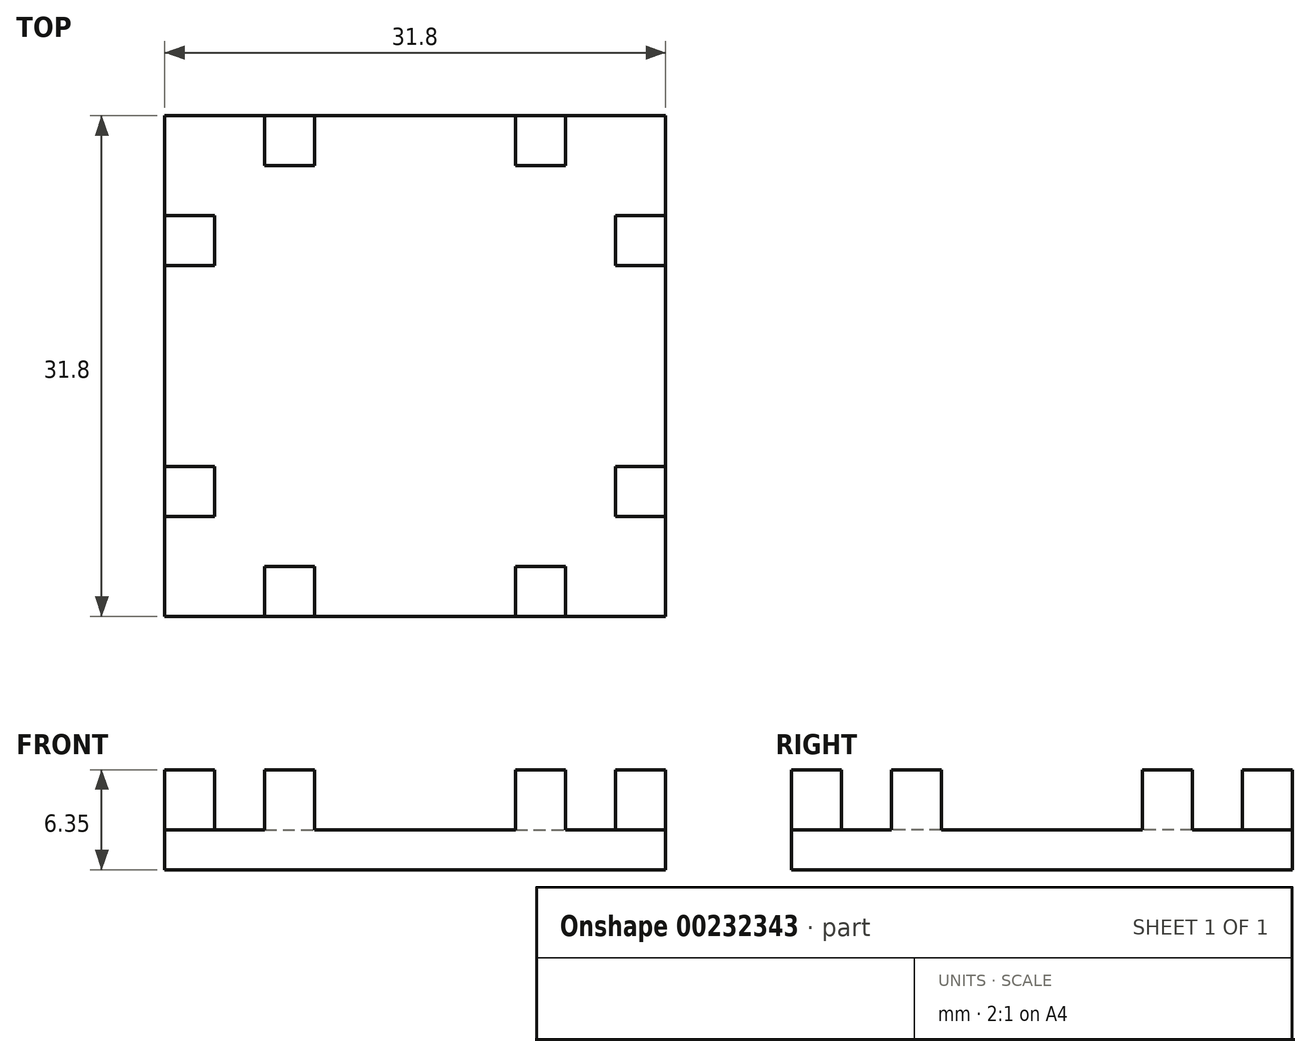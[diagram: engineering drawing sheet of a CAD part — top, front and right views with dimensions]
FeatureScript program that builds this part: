
annotation { "Feature Type Name" : "Feature", "Feature Type Description" : "" }
export const myFeature = defineFeature(function(context is Context, id is Id, definition is map)
    precondition{}
    {
        {
            var Q0;
            Q0=qCreatedBy(makeId("Top.planeOp"),FACE);
            var sketch = newSketch(context, id + "F0", { "sketchPlane" : qUnion([Q0])});
            skLineSegment(sketch, "E0.bottom", {"start": v(15.9, -15.9) * mm, "end": v(-15.9, -15.9) * mm});
            skLineSegment(sketch, "E0.top", {"start": v(15.9, 15.9) * mm, "end": v(-15.9, 15.9) * mm});
            skLineSegment(sketch, "E0.left", {"start": v(15.9, -15.9) * mm, "end": v(15.9, 15.9) * mm});
            skLineSegment(sketch, "E0.right", {"start": v(-15.9, -15.9) * mm, "end": v(-15.9, 15.9) * mm});
            skPoint(sketch, "E0.middle", {"position": v(0, 0) * mm});
            skSolve(sketch);
        }
        {
            var Q0;
            Q0=makeQuery(id+"F0.imprint","IMPRINT",FACE,{"disambiguationData":[TD([[makeQuery(id+"F0.imprint","IMPRINT",EDGE,{"derivedFrom":sQuery(id+"F0.wireOp",EDGE,"E0.bottom")}),-1.0]])]});
            extrude(context, id + "F1", {"entities" : qUnion([Q0]), "oppositeDirection" : true, "depth" : 2.54 * mm});
        }
        {
            var Q0;
            Q0=qCreatedBy(makeId("Top.planeOp"),FACE);
            var sketch = newSketch(context, id + "F2", { "sketchPlane" : qUnion([Q0])});
            skLineSegment(sketch, "E1.bottom", {"start": v(-9.55, 15.9) * mm, "end": v(-6.38, 15.9) * mm});
            skLineSegment(sketch, "E1.top", {"start": v(-9.55, 12.73) * mm, "end": v(-6.38, 12.73) * mm});
            skLineSegment(sketch, "E1.left", {"start": v(-9.55, 15.9) * mm, "end": v(-9.55, 12.73) * mm});
            skLineSegment(sketch, "E1.right", {"start": v(-6.38, 15.9) * mm, "end": v(-6.38, 12.73) * mm});
            skLineSegment(sketch, "E2.bottom", {"start": v(-15.9, 9.55) * mm, "end": v(-12.73, 9.55) * mm});
            skLineSegment(sketch, "E2.top", {"start": v(-15.9, 6.38) * mm, "end": v(-12.73, 6.38) * mm});
            skLineSegment(sketch, "E2.left", {"start": v(-15.9, 9.55) * mm, "end": v(-15.9, 6.38) * mm});
            skLineSegment(sketch, "E2.right", {"start": v(-12.73, 9.55) * mm, "end": v(-12.73, 6.38) * mm});
            skLineSegment(sketch, "E3.bottom", {"start": v(12.73, 9.55) * mm, "end": v(15.9, 9.55) * mm});
            skLineSegment(sketch, "E3.top", {"start": v(12.73, 6.38) * mm, "end": v(15.9, 6.38) * mm});
            skLineSegment(sketch, "E3.left", {"start": v(12.73, 9.55) * mm, "end": v(12.73, 6.38) * mm});
            skLineSegment(sketch, "E3.right", {"start": v(15.9, 9.55) * mm, "end": v(15.9, 6.38) * mm});
            skLineSegment(sketch, "E4.bottom", {"start": v(-15.9, -6.38) * mm, "end": v(-12.73, -6.38) * mm});
            skLineSegment(sketch, "E4.top", {"start": v(-15.9, -9.55) * mm, "end": v(-12.73, -9.55) * mm});
            skLineSegment(sketch, "E4.left", {"start": v(-15.9, -6.38) * mm, "end": v(-15.9, -9.55) * mm});
            skLineSegment(sketch, "E4.right", {"start": v(-12.73, -6.38) * mm, "end": v(-12.73, -9.55) * mm});
            skLineSegment(sketch, "E5.bottom", {"start": v(-9.55, -12.73) * mm, "end": v(-6.38, -12.73) * mm});
            skLineSegment(sketch, "E5.top", {"start": v(-9.55, -15.9) * mm, "end": v(-6.38, -15.9) * mm});
            skLineSegment(sketch, "E5.left", {"start": v(-9.55, -12.73) * mm, "end": v(-9.55, -15.9) * mm});
            skLineSegment(sketch, "E5.right", {"start": v(-6.38, -12.73) * mm, "end": v(-6.38, -15.9) * mm});
            skPoint(sketch, "E6.oppositeSnap0", {"position": v(-7.96, 12.73) * mm});
            skLineSegment(sketch, "E6.bottom", {"start": v(6.38, 15.9) * mm, "end": v(9.55, 15.9) * mm});
            skLineSegment(sketch, "E6.top", {"start": v(6.38, 12.73) * mm, "end": v(9.55, 12.73) * mm});
            skLineSegment(sketch, "E6.left", {"start": v(6.38, 15.9) * mm, "end": v(6.38, 12.73) * mm});
            skLineSegment(sketch, "E6.right", {"start": v(9.55, 15.9) * mm, "end": v(9.55, 12.73) * mm});
            skLineSegment(sketch, "E7.bottom", {"start": v(12.73, -6.38) * mm, "end": v(15.9, -6.38) * mm});
            skLineSegment(sketch, "E7.top", {"start": v(12.73, -9.55) * mm, "end": v(15.9, -9.55) * mm});
            skLineSegment(sketch, "E7.left", {"start": v(12.73, -6.38) * mm, "end": v(12.73, -9.55) * mm});
            skLineSegment(sketch, "E7.right", {"start": v(15.9, -6.38) * mm, "end": v(15.9, -9.55) * mm});
            skLineSegment(sketch, "E8.bottom", {"start": v(6.38, -12.73) * mm, "end": v(9.55, -12.73) * mm});
            skLineSegment(sketch, "E8.top", {"start": v(6.38, -15.9) * mm, "end": v(9.55, -15.9) * mm});
            skLineSegment(sketch, "E8.left", {"start": v(6.38, -12.73) * mm, "end": v(6.38, -15.9) * mm});
            skLineSegment(sketch, "E8.right", {"start": v(9.55, -12.73) * mm, "end": v(9.55, -15.9) * mm});
            skSolve(sketch);
        }
        {
            var Q0;
            Q0=qSketchRegion(id+"F2",true);
            extrude(context, id + "F3", {"entities" : qUnion([Q0]), "operationType" : NewBodyOperationType.ADD, "depth" : 3.8 * mm});
        }
    });
